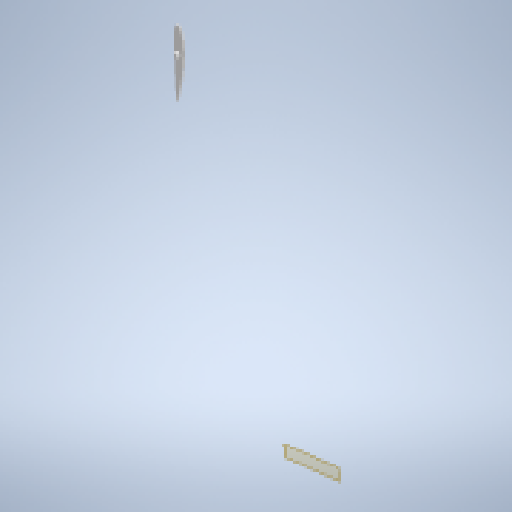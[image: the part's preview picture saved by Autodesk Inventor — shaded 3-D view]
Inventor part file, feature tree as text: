
AUTODESK INVENTOR PART (.ipt)
format: ipt  version: 2025.2 (Build 292293000, 293)  size: 166,400 bytes
history: native  units: in
note: dims shown in document units (in); Inventor stores cm internally (conversion verified against a paired STEP export)
features: other x3, sketch x2, plane x1
ambient origin geometry x8: Origin, YZ Plane, XZ Plane, XY Plane, X Axis, Y Axis, Z Axis, Center Point
bodies: Solid1 (feature_tree)
feature tree (6):
  other  "WingCap.ipt"
  other  "Solid1::WingCap.ipt"
  other  "TaggingFeature1"
  sketch  "Sketch1"  dims[d0=0.3937in]
  sketch  "Sketch2"
  plane  "Work Plane1"
